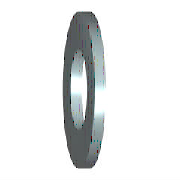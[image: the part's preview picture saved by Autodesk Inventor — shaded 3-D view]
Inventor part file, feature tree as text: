
AUTODESK INVENTOR PART (.ipt)
format: ipt  version: 2024 (Build 280153000, 153)  size: 104,960 bytes
history: native  units: mm (DEFAULTED — no unit token found)
features: extrude x1, other x1, plane x1
ambient origin geometry x7: Origin, YZ Plane, XY Plane, X Axis, Y Axis, Z Axis, Center Point
bodies: Solid1 (feature_tree)
feature tree (3):
  extrude  "Базовый элемент"  Depth=4.3mm
  other  "Work Axis1"
  plane  "Work Plane1"
